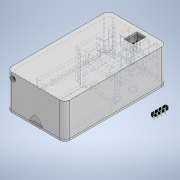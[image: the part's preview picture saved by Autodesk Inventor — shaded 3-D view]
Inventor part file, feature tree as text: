
AUTODESK INVENTOR PART (.ipt)
format: ipt  version: 2022 (Build 260153000, 153)  size: 894,464 bytes
history: native  units: mm
features: sketch x20, extrude x19, fillet x6, other x3, plane x2, chamfer x1, move_body x1, shell x1
ambient origin geometry x8: Origin, YZ Plane, XZ Plane, XY Plane, X Axis, Y Axis, Z Axis, Center Point
bodies: Body1 (feature_tree), Body2 (feature_tree), Body3 (feature_tree), Body4 (feature_tree)
feature tree (53):
  other  "Control"
  extrude  "Extrusion1"  Depth=28.8mm
  extrude  "Extrusion2"  Depth=14.7mm
  extrude  "Extrusion3"  Depth=2.36mm
  extrude  "Extrusion4"  Depth=7.9mm
  extrude  "Extrusion6"  Depth=8.55mm
  extrude  "Extrusion7"  Depth=2.36mm
  chamfer  "Chamfer1"  Distance=8.5mm
  extrude  "Extrusion8"  Depth=10.17mm
  extrude  "Extrusion9"  Depth=11.0mm
  plane  "Work Plane2"
  extrude  "Extrusion10"  Depth=9.44mm
  extrude  "Extrusion11"  Depth=4.82mm
  extrude  "Extrusion12"  Depth=10.0mm
  move_body  "Move Body1"
  plane  "Work Plane4"
  extrude  "Extrusion13"  Depth=0.4mm
  extrude  "Extrusion14"  Depth=11.13mm
  extrude  "Extrusion15"  Depth=0.61mm
  sketch  "Sketch16"  dims[d40=12.7mm d41=11.13mm]
  extrude  "Extrusion16"  Depth=0.61mm
  extrude  "Extrusion17"  Depth=0.61mm
  fillet  "Fillet1"  Radius=0.61mm
  fillet  "Fillet2"  Radius=1.0mm
  fillet  "Fillet3"  Radius=1.0mm
  extrude  "Extrusion18"  Depth=2.085mm
  extrude  "Extrusion19"  Depth=0.925mm
  extrude  "Extrusion20"  Depth=1.0mm TaperAngle=0.0deg
  fillet  "Fillet4"  Radius=2.0mm
  fillet  "Fillet5"  Radius=0.4mm
  fillet  "Fillet6"  Radius=0.2mm
  sketch  "Sketch22"  dims[d56=0.925mm d57=5.8mm d58=0.0mm d59=0.2mm d60=2.0mm d61=45.0deg d62=0.4mm d63=0.2mm d64=0.2mm d65=1.9425mm d66=0.4mm d67=0.4mm d68=0.4mm d69=1.9425mm d70=2.0mm d71=2.0mm d72=2.005mm d73=0.2mm d74=0.2mm d75=0.2mm d76=0.2mm d77=0.2mm d83=2.2mm d84=0.2mm d85=2.2mm d86=2.345mm d90=0.4mm d91=0.4mm d92=0.2mm d93=2.54mm d94=0.0mm d102=0.61mm d103=0.61mm d112=0.2mm d113=0.2mm d114=0.4mm d115=0.2mm d117=2.345mm d118=1.075mm d119=0.875mm d120=0.875mm d121=2.3mm d122=0.61mm d123=0.61mm d124=0.61mm d125=2.3mm d126=2.3mm d127=1.075mm d128=2.65mm d129=0.0mm d130=28.7mm d131=32.7mm d134=1.6mm d135=0.0mm d136=6.0mm d137=6.0mm d138=6.0mm d139=6.0mm d140=2.3mm d141=11.53mm d142=2.6mm d143=6.7mm d144=4.0mm d145=0.0mm d146=3.5mm d147=3.5mm d148=3.5mm d149=3.5mm d150=3.0mm d151=3.0mm d152=3.0mm d153=3.0mm d154=4.55mm d155=-0.349066mm d158=180.0deg d159=5.0mm d160=-14.0mm d161=-8.0mm d162=2.0mm d163=45.0mm d164=3.0mm d165=13.0mm d166=2.5mm d167=7.0mm d168=10.0mm d173=1.5mm d174=0.0mm d175=2.0mm d176=2.0mm d177=2.0mm d178=2.0mm d179=30.0mm d180=0.0mm d181=1.0mm d182=2.0mm d183=22.0mm d184=0.0mm d185=45.813165mm d187=24.5mm d188=2.313165mm d189=4.0mm d190=1.0mm d191=2.0mm d192=2.0mm d193=2.0mm d194=1.0mm d195=2.0mm d197=15.0mm d199=25.0mm d200=11.3mm d201=23.0mm d202=22.813165mm d203=22.0mm d204=-2.094395mm d205=4.0mm d206=5.0mm d207=4.0mm d208=22.0mm d209=0.0mm d210=4.0mm d211=3.0mm d212=1.0mm d213=4.0mm d214=5.0mm d215=5.0mm d216=5.0mm d217=5.0mm d218=1.5mm d219=0.0mm d220=25.0mm d221=11.3mm d222=32.2mm d224=2.0mm d225=2.0mm d226=2.0mm d228=2.0mm d231=1.015mm d232=1.015mm d233=1.0mm d234=1.0mm d235=3.0mm d236=3.0mm d237=35.0mm d238=2.0mm d239=22.0mm d240=6.0mm d241=2.0mm d242=3.5mm d243=0.0mm d244=10.0mm d245=8.0mm d246=3.0mm d247=2.0mm d248=4.0mm d249=0.0mm d250=8.0mm d251=2.0mm d252=5.0mm d253=11.0mm d254=3.0mm d255=2.0mm d256=10.25mm d257=0.0mm d258=1.0mm d259=1.0mm d260=1.0mm]
  sketch  "Sketch1"  dims[d0=29.4mm d1=28.8mm]
  sketch  "Sketch2"  dims[d2=14.4mm d3=14.7mm]
  sketch  "Sketch3"  dims[d4=1.57mm d5=0.0mm d6=2.36mm]
  sketch  "Sketch4"  dims[d7=11.49mm d8=7.9mm]
  sketch  "Sketch6"  dims[d9=0.77mm d10=8.55mm]
  sketch  "Sketch7"  dims[d11=0.6mm d12=2.36mm]
  sketch  "Sketch8"  dims[d13=0.4mm d14=8.5mm d15=0.0mm]
  other  "Buttons"
  sketch  "Sketch9"  dims[d16=10.15mm d17=10.17mm]
  sketch  "Sketch11"  dims[d18=5.0mm d19=11.0mm]
  sketch  "Sketch12"  dims[d20=8.0mm d21=0.0mm d22=9.44mm]
  sketch  "Sketch13"  dims[d23=4.82mm d24=4.82mm]
  sketch  "Sketch14"  dims[d25=7.0mm d26=10.0mm d27=0.0mm d28=0.0mm d37=4.97mm]
  sketch  "Sketch15"  dims[d38=8.0mm d39=0.4mm]
  sketch  "Sketch17"  dims[d42=2.55mm d43=0.0mm d44=0.61mm]
  sketch  "Sketch18"  dims[d45=0.61mm d46=0.61mm]
  sketch  "Sketch19"  dims[d47=0.61mm d48=0.61mm d49=0.61mm d50=1.0mm d51=1.0mm]
  other  "Lid"
  shell  "Shell"  Thickness=0.2mm
  sketch  "Sketch20"  dims[d52=2.085mm d53=2.085mm]
  sketch  "Sketch21"  dims[d54=1.9mm d55=0.925mm]
